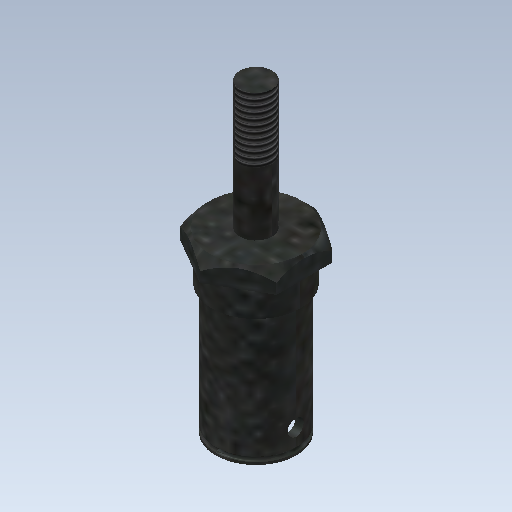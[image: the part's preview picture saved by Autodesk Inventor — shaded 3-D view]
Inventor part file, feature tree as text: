
AUTODESK INVENTOR PART (.ipt)
format: ipt  version: 2020 (Build 240168000, 168)  size: 215,040 bytes
history: native  units: mm
features: sketch x8, extrude x6, revolve x2, thread x1, projected_geometry x1
ambient origin geometry x8: Origin, YZ Plane, XZ Plane, XY Plane, X Axis, Y Axis, Z Axis, Center Point
bodies: Solid1 (feature_tree)
feature tree (18):
  extrude  "Extrusion1"  Depth=2.5mm TaperAngle=0.0deg
  extrude  "Extrusion2"  Depth=15.8mm TaperAngle=0.0deg
  thread  "Thread1"  [1 undecoded]
  extrude  "Extrusion3"  Depth=3.44mm TaperAngle=0.0deg
  extrude  "Extrusion4"  Depth=10.0mm TaperAngle=0.0deg
  extrude  "Extrusion5"  Depth=10.0mm TaperAngle=0.0deg
  extrude  "Extrusion6"  Depth=3.0mm
  revolve  "Revolution1"  [1 undecoded]
  revolve  "Revolution2"  Angle=90.0deg
  sketch  "Sketch1"  dims[d0=12.0mm d1=2.5mm d2=0.0mm]
  sketch  "Sketch2"  dims[d3=4.0mm d4=15.8mm d5=0.0mm d6=8.0mm d7=0.0mm]
  sketch  "Sketch3"  dims[d8=11.0mm d9=3.44mm d10=0.0mm]
  sketch  "Sketch4"  dims[d11=10.0mm d12=16.0mm d13=0.0mm]
  sketch  "Sketch5"  dims[d14=8.0mm d15=10.0mm d16=0.0mm]
  sketch  "Sketch6"  dims[d17=2.0mm d18=3.0mm]
  sketch  "Sketch7"  dims[d19=14.0mm d20=0.0mm d21=0.6mm]
  sketch  "Sketch8"  dims[d22=0.6mm d23=90.0deg d24=45.0deg d25=90.0deg]
  projected_geometry  "Project Cut Edges1"
note: 2 required parameter values undecoded (feature->parameter linkage not recoverable at this tier; creation-order binding heuristic only, values carry confidence <= 0.55)